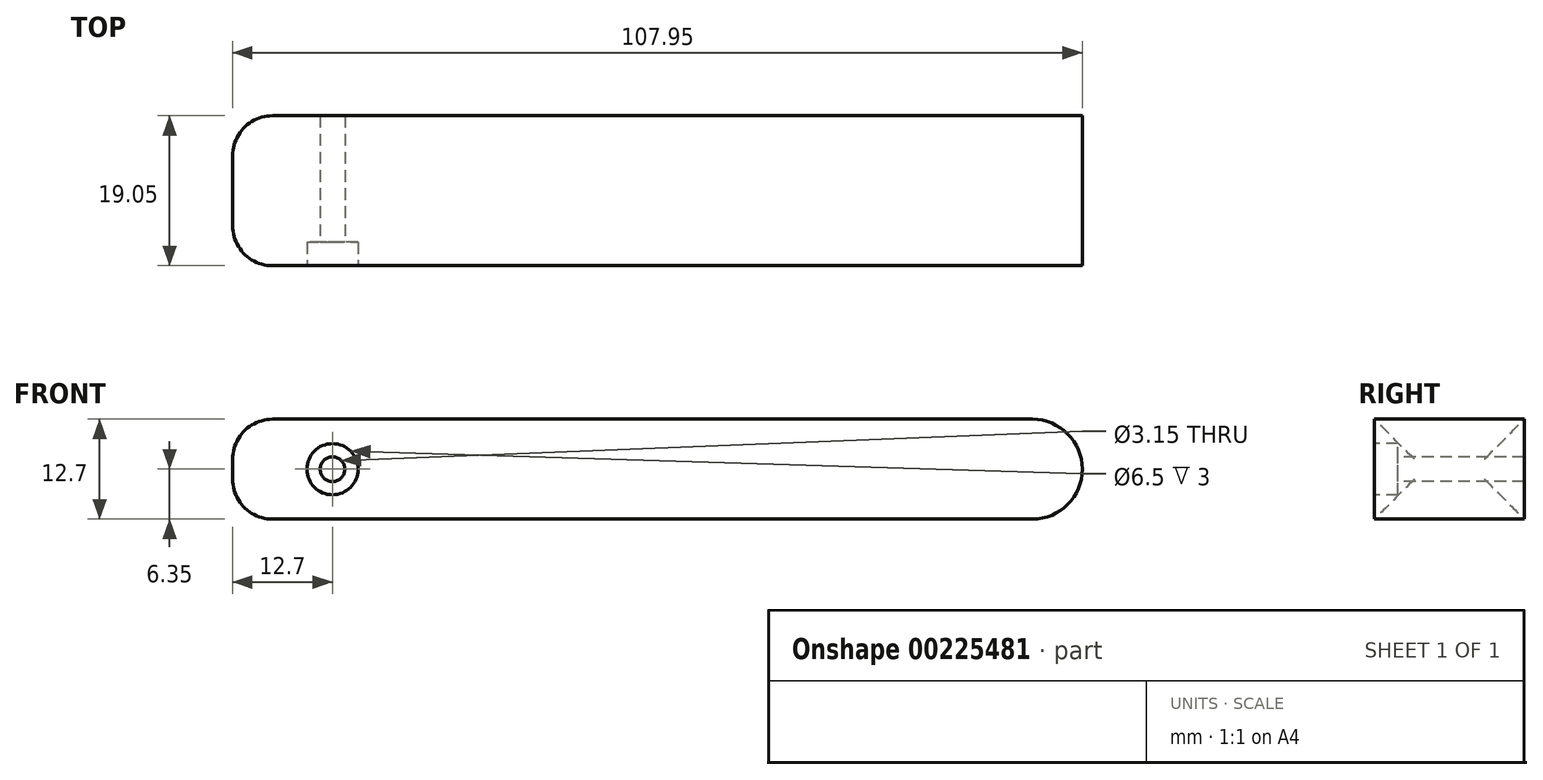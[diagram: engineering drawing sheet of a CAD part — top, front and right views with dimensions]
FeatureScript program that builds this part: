
annotation { "Feature Type Name" : "Feature", "Feature Type Description" : "" }
export const myFeature = defineFeature(function(context is Context, id is Id, definition is map)
    precondition{}
    {
        {
            var Q0;
            Q0=qCreatedBy(makeId("Front.planeOp"),FACE);
            var sketch = newSketch(context, id + "F0", { "sketchPlane" : qUnion([Q0])});
            skLineSegment(sketch, "E0.bottom", {"start": v(0, 0) * mm, "end": v(101.6, 0) * mm});
            skLineSegment(sketch, "E0.top", {"start": v(0, 12.7) * mm, "end": v(101.6, 12.7) * mm});
            skLineSegment(sketch, "E0.left", {"start": v(0, 0) * mm, "end": v(0, 12.7) * mm});
            skArc(sketch, "E1", {"start": v(101.6, 0) * mm, "mid": v(107.95, 6.35) * mm, "end": v(101.6, 12.7) * mm});
            skSolve(sketch);
        }
        {
            var Q0;
            Q0=makeQuery(id+"F0.imprint","IMPRINT",FACE,{"disambiguationData":[TD([[makeQuery(id+"F0.imprint","IMPRINT",EDGE,{"derivedFrom":sQuery(id+"F0.wireOp",EDGE,"E0.bottom")}),1.0]])]});
            extrude(context, id + "F1", {"entities" : qUnion([Q0]), "depth" : 19.05 * mm});
        }
        {
            var Q0;
            Q0=makeQuery(id+"F1.opExtrude","CAP_EDGE",EDGE,{"disambiguationData":[OSD([sQuery(id+"F0.wireOp",EDGE,"E0.left")])],"isStart":false});
            var Q1;
            Q1=makeQuery(id+"F1.opExtrude","SWEPT_EDGE",EDGE,{"disambiguationData":[OSD([sQuery(id+"F0.wireOp",EDGE,"E0.top"),sQuery(id+"F0.wireOp",EDGE,"E0.left")])]});
            var Q2;
            Q2=makeQuery(id+"F1.opExtrude","CAP_EDGE",EDGE,{"disambiguationData":[OSD([sQuery(id+"F0.wireOp",EDGE,"E0.left")])],"isStart":true});
            var Q3;
            Q3=makeQuery(id+"F1.opExtrude","SWEPT_EDGE",EDGE,{"disambiguationData":[OSD([sQuery(id+"F0.wireOp",EDGE,"E0.bottom"),sQuery(id+"F0.wireOp",EDGE,"E0.left")])]});
            fillet(context, id + "F2", {"entities" : qUnion([Q0, Q1, Q2, Q3]), "radius" : 5.08 * mm, "tangentPropagation" : true, "allowEdgeOverflow" : false});
        }
        {
            var Q0;
            Q0=makeQuery(id+"F1.opExtrude","CAP_FACE",FACE,{"disambiguationData":[OSD([sQuery(id+"F0.wireOp",EDGE,"E0.bottom"),sQuery(id+"F0.wireOp",EDGE,"E0.top"),sQuery(id+"F0.wireOp",EDGE,"E0.left"),sQuery(id+"F0.wireOp",EDGE,"E1")])],"isStart":false});
            var sketch = newSketch(context, id + "F3", { "sketchPlane" : qUnion([Q0])});
            skPoint(sketch, "E2", {"position": v(12.7, 6.35) * mm});
            skSolve(sketch);
        }
        {
            var Q0;
            Q0=sQuery(id+"F3.wireOp",VERTEX,"E2");
            var Q1;
            Q1=makeQuery(id+"F1.opExtrude","SWEPT_BODY",BODY,{"disambiguationData":[OSD([sQuery(id+"F0.wireOp",EDGE,"E0.bottom"),sQuery(id+"F0.wireOp",EDGE,"E0.top"),sQuery(id+"F0.wireOp",EDGE,"E0.left"),sQuery(id+"F0.wireOp",EDGE,"E1")])]});
            hole(context, id + "F4", {"style" : HoleStyle.C_BORE, "endStyle" : HoleEndStyle.THROUGH, "standardTappedOrClearance" : lookupTablePath({ "standard" : "ISO", "fit" : "Close", "size" : "M3", "type" : "Clearance" }), "standardBlindInLast" : lookupTablePath({ "fit" : "Close", "standard" : "ISO", "size" : "M3", "type" : "Clearance" }), "holeDiameter" : 3.15 * mm, "cBoreDiameter" : 6.5 * mm, "cBoreDepth" : 3 * mm, "startFromSketch" : true, "locations" : qUnion([Q0]), "scope" : qUnion([Q1]), "isTappedThrough" : true});
        }
    });
